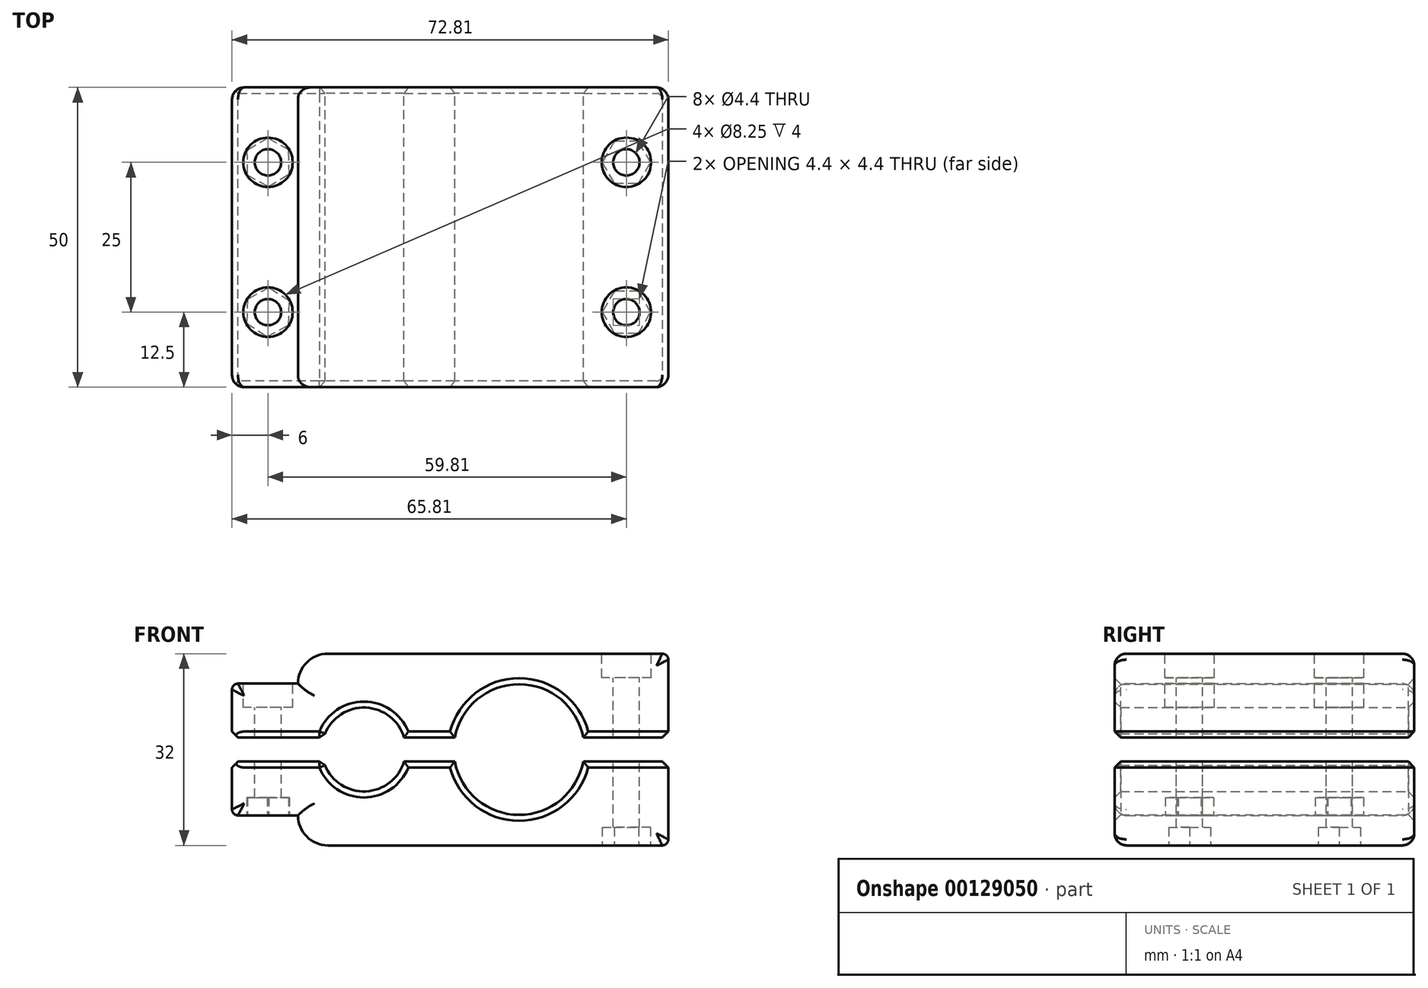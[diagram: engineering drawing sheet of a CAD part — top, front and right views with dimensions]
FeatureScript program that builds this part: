
annotation { "Feature Type Name" : "Feature", "Feature Type Description" : "" }
export const myFeature = defineFeature(function(context is Context, id is Id, definition is map)
    precondition{}
    {
        {
            var Q0;
            Q0=qCreatedBy(makeId("Front.planeOp"),FACE);
            var sketch = newSketch(context, id + "F0", { "sketchPlane" : qUnion([Q0])});
            skLineSegment(sketch, "E0.left", {"start": v(0, 26.04) * mm, "end": v(0, 18.04) * mm});
            skLineSegment(sketch, "E0.right", {"start": v(72.8, 31.04) * mm, "end": v(72.8, 18.04) * mm});
            skLineSegment(sketch, "E1", {"start": v(10.56, 16.04) * mm, "end": v(72.8, 16.04) * mm, "construction": true});
            skArc(sketch, "E2", {"start": v(15.3, 14.04) * mm, "mid": v(22, 9.04) * mm, "end": v(28.7, 14.04) * mm});
            skArc(sketch, "E3", {"start": v(37.18, 14.04) * mm, "mid": v(47.9, 5.14) * mm, "end": v(58.63, 14.04) * mm});
            skCircle(sketch, "E4", {"center": v(22, 16.04) * mm, "radius": 11.44 * mm, "construction": true});
            skLineSegment(sketch, "E5.bottom", {"start": v(0, 18.04) * mm, "end": v(15.3, 18.04) * mm});
            skLineSegment(sketch, "E5.top", {"start": v(0, 14.04) * mm, "end": v(15.3, 14.04) * mm});
            skLineSegment(sketch, "E6.trimOffspring", {"start": v(0, 14.04) * mm, "end": v(0, 5.04) * mm});
            skArc(sketch, "E7.trimOffspring", {"start": v(28.7, 18.04) * mm, "mid": v(22, 23.04) * mm, "end": v(15.3, 18.04) * mm});
            skPoint(sketch, "E8.orphan", {"position": v(0, 16.04) * mm});
            skPoint(sketch, "E9", {"position": v(4.76, 32) * mm});
            skCircle(sketch, "E10", {"center": v(47.9, 16.04) * mm, "radius": 10.78 * mm, "construction": true});
            skCircle(sketch, "E11", {"center": v(22, 16.04) * mm, "radius": 6.5 * mm, "construction": true});
            skLineSegment(sketch, "E12.bottom", {"start": v(1, 27.04) * mm, "end": v(11, 27.04) * mm});
            skLineSegment(sketch, "E12.top", {"start": v(1, 5.04) * mm, "end": v(11, 5.04) * mm});
            skLineSegment(sketch, "E12.left", {"start": v(0, 27.04) * mm, "end": v(0, 18.04) * mm});
            skLineSegment(sketch, "E13.bottom", {"start": v(1.99, 39.63) * mm, "end": v(5.99, 39.63) * mm, "construction": true});
            skLineSegment(sketch, "E13.top", {"start": v(1.99, -10.37) * mm, "end": v(5.99, -10.37) * mm, "construction": true});
            skLineSegment(sketch, "E13.left", {"start": v(1.99, 39.63) * mm, "end": v(1.99, -10.37) * mm, "construction": true});
            skLineSegment(sketch, "E13.right", {"start": v(5.99, 39.63) * mm, "end": v(5.99, -10.37) * mm, "construction": true});
            skLineSegment(sketch, "E14", {"start": v(11, 27.04) * mm, "end": v(11, 27.04) * mm});
            skLineSegment(sketch, "E15", {"start": v(11, 5.04) * mm, "end": v(11, 5) * mm});
            skLineSegment(sketch, "E16.trimOffspring", {"start": v(16, 32.04) * mm, "end": v(71.8, 32.04) * mm});
            skPoint(sketch, "E17.orphan", {"position": v(0, 32.09) * mm});
            skLineSegment(sketch, "E18.trimOffspring", {"start": v(16, 0) * mm, "end": v(71.81, 0.04) * mm});
            skPoint(sketch, "E19.orphan", {"position": v(0, 0) * mm});
            skLineSegment(sketch, "E20.trimOffspring", {"start": v(0, 14.04) * mm, "end": v(0, 6.04) * mm});
            skPoint(sketch, "E21.visualSharp", {"position": v(11, 32.04) * mm});
            skArc(sketch, "E21.filletArc", {"start": v(16, 32.04) * mm, "mid": v(12.46, 30.58) * mm, "end": v(11, 27.04) * mm});
            skPoint(sketch, "E22.visualSharp", {"position": v(11, 0) * mm});
            skArc(sketch, "E22.filletArc", {"start": v(11, 5) * mm, "mid": v(12.47, 1.47) * mm, "end": v(16, 0) * mm});
            skPoint(sketch, "E23.visualSharp", {"position": v(0, 27.04) * mm});
            skArc(sketch, "E23.filletArc", {"start": v(1, 27.04) * mm, "mid": v(0.3, 26.75) * mm, "end": v(0, 26.04) * mm});
            skPoint(sketch, "E24.visualSharp", {"position": v(0, 18.04) * mm});
            skLineSegment(sketch, "E24.filletArc", {"start": v(0, 18.04) * mm, "end": v(0, 18.04) * mm});
            skPoint(sketch, "E25.visualSharp", {"position": v(72.8, 32.04) * mm});
            skArc(sketch, "E25.filletArc", {"start": v(72.8, 31.04) * mm, "mid": v(72.52, 31.75) * mm, "end": v(71.8, 32.04) * mm});
            skPoint(sketch, "E26.visualSharp", {"position": v(72.8, 0.04) * mm});
            skArc(sketch, "E26.filletArc", {"start": v(71.81, 0.04) * mm, "mid": v(72.52, 0.34) * mm, "end": v(72.8, 1.04) * mm});
            skPoint(sketch, "E27.visualSharp", {"position": v(0, 5.04) * mm});
            skArc(sketch, "E27.filletArc", {"start": v(0, 6.04) * mm, "mid": v(0.3, 5.34) * mm, "end": v(1, 5.04) * mm});
            skLineSegment(sketch, "E28.trimOffspring", {"start": v(28.7, 18.04) * mm, "end": v(37.31, 18.04) * mm});
            skLineSegment(sketch, "E29.trimOffspring", {"start": v(28.7, 14.04) * mm, "end": v(37.31, 14.04) * mm});
            skLineSegment(sketch, "E30.trimOffspring", {"start": v(58.5, 14.04) * mm, "end": v(58.63, 14.04) * mm});
            skLineSegment(sketch, "E31.trimOffspring", {"start": v(58.5, 18.04) * mm, "end": v(58.63, 18.04) * mm});
            skLineSegment(sketch, "E32.bottom", {"start": v(72.8, 14.04) * mm, "end": v(58.5, 14.04) * mm});
            skLineSegment(sketch, "E32.top", {"start": v(72.8, 18.04) * mm, "end": v(58.5, 18.04) * mm});
            skPoint(sketch, "E32.middle", {"position": v(66.12, 16.04) * mm});
            skArc(sketch, "E33.trimOffspring", {"start": v(58.63, 18.04) * mm, "mid": v(47.9, 26.95) * mm, "end": v(37.18, 18.04) * mm});
            skPoint(sketch, "E34.orphan", {"position": v(57.58, 14.04) * mm});
            skLineSegment(sketch, "E35.trimOffspring", {"start": v(72.8, 14.04) * mm, "end": v(72.8, 1.04) * mm});
            skSolve(sketch);
        }
        {
            var Q0;
            Q0=makeQuery(id+"F0.imprint","IMPRINT",FACE,{"disambiguationData":[TD([[makeQuery(id+"F0.imprint","IMPRINT",EDGE,{"derivedFrom":sQuery(id+"F0.wireOp",EDGE,"E0.right")}),-1.0]])]});
            extrude(context, id + "F1", {"entities" : qUnion([Q0]), "depth" : 50 * mm});
        }
        {
            var Q0;
            Q0=makeQuery(id+"F1.opExtrude","SWEPT_FACE",FACE,{"disambiguationData":[OSD([sQuery(id+"F0.wireOp",EDGE,"E16.trimOffspring")])]});
            fillet(context, id + "F2", {"entities" : qUnion([Q0]), "radius" : 2 * mm, "tangentPropagation" : true, "allowEdgeOverflow" : false});
        }
        {
            var Q0;
            Q0=makeQuery(id+"F1.opExtrude","CAP_EDGE",EDGE,{"disambiguationData":[OSD([sQuery(id+"F0.wireOp",EDGE,"E3")])],"isStart":false});
            var Q1;
            Q1=makeQuery(id+"F1.opExtrude","CAP_EDGE",EDGE,{"disambiguationData":[OSD([sQuery(id+"F0.wireOp",EDGE,"E7.trimOffspring")])],"isStart":false});
            var Q2;
            Q2=makeQuery(id+"F1.opExtrude","CAP_EDGE",EDGE,{"disambiguationData":[OSD([sQuery(id+"F0.wireOp",EDGE,"E2")])],"isStart":false});
            var Q3;
            Q3=makeQuery(id+"F1.opExtrude","CAP_EDGE",EDGE,{"disambiguationData":[OSD([sQuery(id+"F0.wireOp",EDGE,"E5.bottom")])],"isStart":false});
            var Q4;
            Q4=makeQuery(id+"F1.opExtrude","CAP_EDGE",EDGE,{"disambiguationData":[OSD([sQuery(id+"F0.wireOp",EDGE,"E5.top")])],"isStart":false});
            var Q5;
            Q5=makeQuery(id+"F1.opExtrude","CAP_EDGE",EDGE,{"disambiguationData":[OSD([sQuery(id+"F0.wireOp",EDGE,"E28.trimOffspring")])],"isStart":false});
            var Q6;
            Q6=makeQuery(id+"F1.opExtrude","CAP_EDGE",EDGE,{"disambiguationData":[OSD([sQuery(id+"F0.wireOp",EDGE,"E29.trimOffspring")])],"isStart":false});
            var Q7;
            Q7=makeQuery(id+"F1.opExtrude","CAP_EDGE",EDGE,{"disambiguationData":[OSD([sQuery(id+"F0.wireOp",EDGE,"E3")])],"isStart":true});
            var Q8;
            Q8=makeQuery(id+"F1.opExtrude","CAP_EDGE",EDGE,{"disambiguationData":[OSD([sQuery(id+"F0.wireOp",EDGE,"E28.trimOffspring")])],"isStart":true});
            var Q9;
            Q9=makeQuery(id+"F1.opExtrude","CAP_EDGE",EDGE,{"disambiguationData":[OSD([sQuery(id+"F0.wireOp",EDGE,"E29.trimOffspring")])],"isStart":true});
            var Q10;
            Q10=makeQuery(id+"F1.opExtrude","CAP_EDGE",EDGE,{"disambiguationData":[OSD([sQuery(id+"F0.wireOp",EDGE,"E7.trimOffspring")])],"isStart":true});
            var Q11;
            Q11=makeQuery(id+"F1.opExtrude","CAP_EDGE",EDGE,{"disambiguationData":[OSD([sQuery(id+"F0.wireOp",EDGE,"E2")])],"isStart":true});
            var Q12;
            Q12=makeQuery(id+"F1.opExtrude","CAP_EDGE",EDGE,{"disambiguationData":[OSD([sQuery(id+"F0.wireOp",EDGE,"E5.bottom")])],"isStart":true});
            var Q13;
            Q13=makeQuery(id+"F1.opExtrude","CAP_EDGE",EDGE,{"disambiguationData":[OSD([sQuery(id+"F0.wireOp",EDGE,"E5.top")])],"isStart":true});
            var Q14;
            Q14=makeQuery(id+"F1.opExtrude","CAP_EDGE",EDGE,{"disambiguationData":[OSD([sQuery(id+"F0.wireOp",EDGE,"E33.trimOffspring")])],"isStart":false});
            var Q15;
            Q15=makeQuery(id+"F1.opExtrude","CAP_EDGE",EDGE,{"disambiguationData":[OSD([sQuery(id+"F0.wireOp",EDGE,"E33.trimOffspring")])],"isStart":true});
            var Q16;
            Q16=makeQuery(id+"F1.opExtrude","CAP_EDGE",EDGE,{"disambiguationData":[OSD([sQuery(id+"F0.wireOp",EDGE,"E32.top")])],"isStart":false});
            var Q17;
            Q17=makeQuery(id+"F1.opExtrude","SWEPT_EDGE",EDGE,{"disambiguationData":[OSD([sQuery(id+"F0.wireOp",EDGE,"E5.bottom"),sQuery(id+"F0.wireOp",EDGE,"E12.left")])]});
            chamfer(context, id + "F3", {"entities" : qUnion([Q0, Q1, Q2, Q3, Q4, Q5, Q6, Q7, Q8, Q9, Q10, Q11, Q12, Q13, Q14, Q15, Q16, Q17]), "width" : 1 * mm, "tangentPropagation" : true});
        }
        {
            var Q0;
            Q0=makeQuery(id+"F1.opExtrude","CAP_EDGE",EDGE,{"disambiguationData":[OSD([sQuery(id+"F0.wireOp",EDGE,"E12.bottom")])],"isStart":false});
            var Q1;
            Q1=makeQuery(id+"F1.opExtrude","CAP_EDGE",EDGE,{"disambiguationData":[OSD([sQuery(id+"F0.wireOp",EDGE,"E12.bottom")])],"isStart":true});
            var Q2;
            Q2=makeQuery(id+"F1.opExtrude","CAP_EDGE",EDGE,{"disambiguationData":[OSD([sQuery(id+"F0.wireOp",EDGE,"E12.top")])],"isStart":false});
            var Q3;
            Q3=makeQuery(id+"F1.opExtrude","CAP_EDGE",EDGE,{"disambiguationData":[OSD([sQuery(id+"F0.wireOp",EDGE,"E12.top")])],"isStart":true});
            fillet(context, id + "F4", {"entities" : qUnion([Q0, Q1, Q2, Q3]), "radius" : 2 * mm, "tangentPropagation" : true, "allowEdgeOverflow" : false});
        }
        {
            var Q0;
            Q0=makeQuery(id+"F1.opExtrude","SWEPT_FACE",FACE,{"disambiguationData":[OSD([sQuery(id+"F0.wireOp",EDGE,"E28.trimOffspring")])]});
            cPlane(context, id + "F5", {"entities" : qUnion([Q0]), "cplaneType" : CPlaneType.OFFSET, "offset" : 2 * mm, "width" : 150 * mm, "height" : 150 * mm});
        }
        {
            var Q0;
            Q0=makeQuery(id+"F1.opExtrude","SWEPT_BODY",BODY,{"disambiguationData":[OSD([sQuery(id+"F0.wireOp",EDGE,"E0.right"),sQuery(id+"F0.wireOp",EDGE,"E5.bottom"),sQuery(id+"F0.wireOp",EDGE,"E7.trimOffspring"),sQuery(id+"F0.wireOp",EDGE,"E12.bottom"),sQuery(id+"F0.wireOp",EDGE,"E12.left"),sQuery(id+"F0.wireOp",EDGE,"E16.trimOffspring"),sQuery(id+"F0.wireOp",EDGE,"E21.filletArc"),sQuery(id+"F0.wireOp",EDGE,"E23.filletArc"),sQuery(id+"F0.wireOp",EDGE,"E25.filletArc"),sQuery(id+"F0.wireOp",EDGE,"E28.trimOffspring"),sQuery(id+"F0.wireOp",EDGE,"E32.top"),sQuery(id+"F0.wireOp",EDGE,"E33.trimOffspring")])]});
            var Q1;
            Q1=qCreatedBy(id+"F5.planeOp",FACE);
            mirror(context, id + "F6", {"entities" : qUnion([Q0]), "mirrorPlane" : qUnion([Q1])});
        }
        {
            var Q0;
            Q0=makeQuery(id+"F1.opExtrude","SWEPT_FACE",FACE,{"disambiguationData":[OSD([sQuery(id+"F0.wireOp",EDGE,"E12.bottom")])]});
            var sketch = newSketch(context, id + "F7", { "sketchPlane" : qUnion([Q0])});
            skLineSegment(sketch, "E36", {"start": v(1, -25) * mm, "end": v(11, -25) * mm, "construction": true});
            skPoint(sketch, "E37", {"position": v(6, -12.5) * mm});
            skPoint(sketch, "E38.MirrorP", {"position": v(6, -37.5) * mm});
            skSolve(sketch);
        }
        {
            var Q0;
            Q0=sQuery(id+"F7.wireOp",VERTEX,"E37");
            var Q1;
            Q1=sQuery(id+"F7.wireOp",VERTEX,"E38.MirrorP");
            var Q2;
            Q2=makeQuery(id+"F1.opExtrude","SWEPT_BODY",BODY,{"disambiguationData":[OSD([sQuery(id+"F0.wireOp",EDGE,"E0.right"),sQuery(id+"F0.wireOp",EDGE,"E5.bottom"),sQuery(id+"F0.wireOp",EDGE,"E7.trimOffspring"),sQuery(id+"F0.wireOp",EDGE,"E12.bottom"),sQuery(id+"F0.wireOp",EDGE,"E12.left"),sQuery(id+"F0.wireOp",EDGE,"E16.trimOffspring"),sQuery(id+"F0.wireOp",EDGE,"E21.filletArc"),sQuery(id+"F0.wireOp",EDGE,"E23.filletArc"),sQuery(id+"F0.wireOp",EDGE,"E25.filletArc"),sQuery(id+"F0.wireOp",EDGE,"E28.trimOffspring"),sQuery(id+"F0.wireOp",EDGE,"E32.top"),sQuery(id+"F0.wireOp",EDGE,"E33.trimOffspring")])]});
            var Q3;
            Q3=makeQuery(id+"F6.opPattern","COPY",BODY,{"derivedFrom":makeQuery(id+"F1.opExtrude","SWEPT_BODY",BODY,{"disambiguationData":[OSD([sQuery(id+"F0.wireOp",EDGE,"E0.right"),sQuery(id+"F0.wireOp",EDGE,"E5.bottom"),sQuery(id+"F0.wireOp",EDGE,"E7.trimOffspring"),sQuery(id+"F0.wireOp",EDGE,"E12.bottom"),sQuery(id+"F0.wireOp",EDGE,"E12.left"),sQuery(id+"F0.wireOp",EDGE,"E16.trimOffspring"),sQuery(id+"F0.wireOp",EDGE,"E21.filletArc"),sQuery(id+"F0.wireOp",EDGE,"E23.filletArc"),sQuery(id+"F0.wireOp",EDGE,"E25.filletArc"),sQuery(id+"F0.wireOp",EDGE,"E28.trimOffspring"),sQuery(id+"F0.wireOp",EDGE,"E32.top"),sQuery(id+"F0.wireOp",EDGE,"E33.trimOffspring")])]}),"instanceName":"1"});
            hole(context, id + "F8", {"style" : HoleStyle.C_BORE, "endStyle" : HoleEndStyle.THROUGH, "standardTappedOrClearance" : lookupTablePath({ "standard" : "ISO", "fit" : "Normal", "size" : "M4", "type" : "Clearance" }), "standardBlindInLast" : lookupTablePath({ "fit" : "Standard", "standard" : "ISO", "size" : "M4", "type" : "Clearance" }), "holeDiameter" : 4.4 * mm, "cBoreDiameter" : 8.25 * mm, "cBoreDepth" : 4 * mm, "locations" : qUnion([Q0, Q1]), "scope" : qUnion([Q2, Q3]), "isTappedThrough" : true});
        }
        {
            var Q0;
            Q0=makeQuery(id+"F1.opExtrude","SWEPT_FACE",FACE,{"disambiguationData":[OSD([sQuery(id+"F0.wireOp",EDGE,"E16.trimOffspring")])]});
            var sketch = newSketch(context, id + "F9", { "sketchPlane" : qUnion([Q0])});
            skPoint(sketch, "E39", {"position": v(65.8, -37.5) * mm});
            skLineSegment(sketch, "E40", {"start": v(72.8, -25) * mm, "end": v(58.63, -25) * mm, "construction": true});
            skPoint(sketch, "E41.MirrorP", {"position": v(65.8, -12.5) * mm});
            skSolve(sketch);
        }
        {
            var Q0;
            Q0=sQuery(id+"F9.wireOp",VERTEX,"E41.MirrorP");
            var Q1;
            Q1=sQuery(id+"F9.wireOp",VERTEX,"E39");
            var Q2;
            Q2=makeQuery(id+"F1.opExtrude","SWEPT_BODY",BODY,{"disambiguationData":[OSD([sQuery(id+"F0.wireOp",EDGE,"E0.right"),sQuery(id+"F0.wireOp",EDGE,"E5.bottom"),sQuery(id+"F0.wireOp",EDGE,"E7.trimOffspring"),sQuery(id+"F0.wireOp",EDGE,"E12.bottom"),sQuery(id+"F0.wireOp",EDGE,"E12.left"),sQuery(id+"F0.wireOp",EDGE,"E16.trimOffspring"),sQuery(id+"F0.wireOp",EDGE,"E21.filletArc"),sQuery(id+"F0.wireOp",EDGE,"E23.filletArc"),sQuery(id+"F0.wireOp",EDGE,"E25.filletArc"),sQuery(id+"F0.wireOp",EDGE,"E28.trimOffspring"),sQuery(id+"F0.wireOp",EDGE,"E32.top"),sQuery(id+"F0.wireOp",EDGE,"E33.trimOffspring")])]});
            var Q3;
            Q3=makeQuery(id+"F6.opPattern","COPY",BODY,{"derivedFrom":makeQuery(id+"F1.opExtrude","SWEPT_BODY",BODY,{"disambiguationData":[OSD([sQuery(id+"F0.wireOp",EDGE,"E0.right"),sQuery(id+"F0.wireOp",EDGE,"E5.bottom"),sQuery(id+"F0.wireOp",EDGE,"E7.trimOffspring"),sQuery(id+"F0.wireOp",EDGE,"E12.bottom"),sQuery(id+"F0.wireOp",EDGE,"E12.left"),sQuery(id+"F0.wireOp",EDGE,"E16.trimOffspring"),sQuery(id+"F0.wireOp",EDGE,"E21.filletArc"),sQuery(id+"F0.wireOp",EDGE,"E23.filletArc"),sQuery(id+"F0.wireOp",EDGE,"E25.filletArc"),sQuery(id+"F0.wireOp",EDGE,"E28.trimOffspring"),sQuery(id+"F0.wireOp",EDGE,"E32.top"),sQuery(id+"F0.wireOp",EDGE,"E33.trimOffspring")])]}),"instanceName":"1"});
            hole(context, id + "F10", {"style" : HoleStyle.C_BORE, "endStyle" : HoleEndStyle.THROUGH, "standardTappedOrClearance" : lookupTablePath({ "standard" : "ISO", "fit" : "Normal", "size" : "M4", "type" : "Clearance" }), "standardBlindInLast" : lookupTablePath({ "fit" : "Standard", "standard" : "ISO", "size" : "M4", "type" : "Clearance" }), "holeDiameter" : 4.4 * mm, "cBoreDiameter" : 8.25 * mm, "cBoreDepth" : 4 * mm, "locations" : qUnion([Q0, Q1]), "scope" : qUnion([Q2, Q3]), "isTappedThrough" : true});
        }
        {
            var Q0;
            Q0=makeQuery(id+"F6.opPattern","COPY",FACE,{"derivedFrom":makeQuery(id+"F1.opExtrude","SWEPT_FACE",FACE,{"disambiguationData":[OSD([sQuery(id+"F0.wireOp",EDGE,"E16.trimOffspring")])]}),"instanceName":"1"});
            var sketch = newSketch(context, id + "F11", { "sketchPlane" : qUnion([Q0])});
            skCircle(sketch, "E42", {"center": v(65.8, 37.5) * mm, "radius": 3.5 * mm, "construction": true});
            skCircle(sketch, "E43", {"center": v(65.8, 12.5) * mm, "radius": 3.5 * mm, "construction": true});
            skLineSegment(sketch, "E44.0", {"start": v(67.83, 34) * mm, "end": v(63.79, 34) * mm});
            skLineSegment(sketch, "E44.1", {"start": v(63.79, 34) * mm, "end": v(61.77, 37.5) * mm});
            skLineSegment(sketch, "E44.2", {"start": v(61.77, 37.5) * mm, "end": v(63.79, 41) * mm});
            skLineSegment(sketch, "E44.3", {"start": v(63.79, 41) * mm, "end": v(67.83, 41) * mm});
            skLineSegment(sketch, "E44.4", {"start": v(67.83, 41) * mm, "end": v(69.85, 37.5) * mm});
            skLineSegment(sketch, "E44.5", {"start": v(69.85, 37.5) * mm, "end": v(67.83, 34) * mm});
            skPoint(sketch, "E44.0.midPoint", {"position": v(65.8, 34) * mm});
            skLineSegment(sketch, "E45.0", {"start": v(67.83, 9) * mm, "end": v(63.79, 9) * mm});
            skLineSegment(sketch, "E45.1", {"start": v(63.79, 9) * mm, "end": v(61.77, 12.5) * mm});
            skLineSegment(sketch, "E45.2", {"start": v(61.77, 12.5) * mm, "end": v(63.79, 16) * mm});
            skLineSegment(sketch, "E45.3", {"start": v(63.79, 16) * mm, "end": v(67.83, 16) * mm});
            skLineSegment(sketch, "E45.4", {"start": v(67.83, 16) * mm, "end": v(69.85, 12.5) * mm});
            skLineSegment(sketch, "E45.5", {"start": v(69.85, 12.5) * mm, "end": v(67.83, 9) * mm});
            skPoint(sketch, "E45.0.midPoint", {"position": v(65.8, 9) * mm});
            skSolve(sketch);
        }
        {
            var Q0;
            Q0 = qSketchRegion(id + "F11", true);
            extrude(context, id + "F12", {"entities" : qUnion([Q0]), "operationType" : NewBodyOperationType.REMOVE, "oppositeDirection" : true, "depth" : 3 * mm});
        }
        {
            var Q0;
            Q0=makeQuery(id+"F6.opPattern","COPY",FACE,{"derivedFrom":makeQuery(id+"F1.opExtrude","SWEPT_FACE",FACE,{"disambiguationData":[OSD([sQuery(id+"F0.wireOp",EDGE,"E12.bottom")])]}),"instanceName":"1"});
            var sketch = newSketch(context, id + "F13", { "sketchPlane" : qUnion([Q0])});
            skCircle(sketch, "E46.cCircle", {"center": v(6, 37.5) * mm, "radius": 3.5 * mm, "construction": true});
            skLineSegment(sketch, "E46.0", {"start": v(9.57, 35.6) * mm, "end": v(6.14, 33.46) * mm});
            skLineSegment(sketch, "E46.1", {"start": v(6.14, 33.46) * mm, "end": v(2.57, 35.36) * mm});
            skLineSegment(sketch, "E46.2", {"start": v(2.57, 35.36) * mm, "end": v(2.43, 39.4) * mm});
            skLineSegment(sketch, "E46.3", {"start": v(2.43, 39.4) * mm, "end": v(5.86, 41.54) * mm});
            skLineSegment(sketch, "E46.4", {"start": v(5.86, 41.54) * mm, "end": v(9.43, 39.64) * mm});
            skLineSegment(sketch, "E46.5", {"start": v(9.43, 39.64) * mm, "end": v(9.57, 35.6) * mm});
            skPoint(sketch, "E46.0.midPoint", {"position": v(7.85, 34.53) * mm});
            skCircle(sketch, "E47.cCircle", {"center": v(6, 12.5) * mm, "radius": 3.5 * mm, "construction": true});
            skLineSegment(sketch, "E47.0", {"start": v(9.46, 10.41) * mm, "end": v(5.92, 8.46) * mm});
            skLineSegment(sketch, "E47.1", {"start": v(5.92, 8.46) * mm, "end": v(2.46, 10.55) * mm});
            skLineSegment(sketch, "E47.2", {"start": v(2.46, 10.55) * mm, "end": v(2.54, 14.59) * mm});
            skLineSegment(sketch, "E47.3", {"start": v(2.54, 14.59) * mm, "end": v(6.08, 16.54) * mm});
            skLineSegment(sketch, "E47.4", {"start": v(6.08, 16.54) * mm, "end": v(9.54, 14.45) * mm});
            skLineSegment(sketch, "E47.5", {"start": v(9.54, 14.45) * mm, "end": v(9.46, 10.41) * mm});
            skPoint(sketch, "E47.0.midPoint", {"position": v(7.69, 9.43) * mm});
            skSolve(sketch);
        }
        {
            var Q0;
            Q0=makeQuery(id+"F13.imprint","IMPRINT",FACE,{"disambiguationData":[TD([[makeQuery(id+"F13.imprint","IMPRINT",EDGE,{"derivedFrom":makeQuery(id+"F8.hole-0.boolean.opBoolean","INTERSECT",EDGE,{"derivedFrom":[makeQuery(id+"F6.opPattern","COPY",FACE,{"derivedFrom":makeQuery(id+"F1.opExtrude","SWEPT_FACE",FACE,{"disambiguationData":[OSD([sQuery(id+"F0.wireOp",EDGE,"E12.bottom")])]}),"instanceName":"1"}),makeQuery(id+"F8.hole-0.opRevolve","SWEPT_FACE",FACE,{"disambiguationData":[OSD([sQuery(id+"F8.hole-0.sketch.wireOp",EDGE,"core_line_2")])]})]})}),-1.0]])]});
            var Q1;
            Q1=makeQuery(id+"F13.imprint","IMPRINT",FACE,{"disambiguationData":[TD([[makeQuery(id+"F13.imprint","IMPRINT",EDGE,{"derivedFrom":makeQuery(id+"F8.hole-1.boolean.opBoolean","INTERSECT",EDGE,{"derivedFrom":[makeQuery(id+"F6.opPattern","COPY",FACE,{"derivedFrom":makeQuery(id+"F1.opExtrude","SWEPT_FACE",FACE,{"disambiguationData":[OSD([sQuery(id+"F0.wireOp",EDGE,"E12.bottom")])]}),"instanceName":"1"}),makeQuery(id+"F8.hole-1.opRevolve","SWEPT_FACE",FACE,{"disambiguationData":[OSD([sQuery(id+"F8.hole-1.sketch.wireOp",EDGE,"core_line_2")])]})]})}),-1.0]])]});
            var Q2;
            Q2=makeQuery(id+"F13.imprint","IMPRINT",FACE,{"disambiguationData":[TD([[makeQuery(id+"F13.imprint","IMPRINT",EDGE,{"derivedFrom":sQuery(id+"F13.wireOp",EDGE,"E47.0")}),-1.0]])]});
            var Q3;
            Q3=makeQuery(id+"F13.imprint","IMPRINT",FACE,{"disambiguationData":[TD([[makeQuery(id+"F13.imprint","IMPRINT",EDGE,{"derivedFrom":sQuery(id+"F13.wireOp",EDGE,"E46.0")}),-1.0]])]});
            extrude(context, id + "F14", {"entities" : qUnion([Q0, Q1, Q2, Q3]), "operationType" : NewBodyOperationType.REMOVE, "oppositeDirection" : true, "depth" : 3 * mm});
        }
    });
